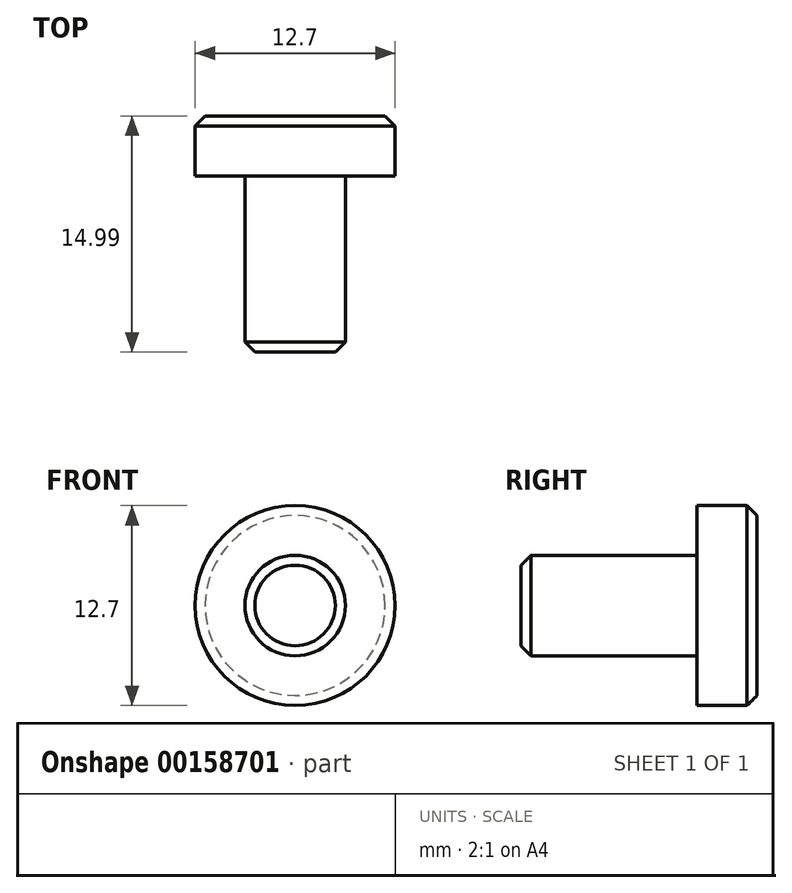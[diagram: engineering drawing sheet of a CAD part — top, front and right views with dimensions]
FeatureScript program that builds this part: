
annotation { "Feature Type Name" : "Feature", "Feature Type Description" : "" }
export const myFeature = defineFeature(function(context is Context, id is Id, definition is map)
    precondition{}
    {
        {
            var Q0;
            Q0=qCreatedBy(makeId("Right.planeOp"),FACE);
            var sketch = newSketch(context, id + "F0", { "sketchPlane" : qUnion([Q0])});
            skLineSegment(sketch, "E0", {"start": v(0, 0) * mm, "end": v(-14.99, 0) * mm});
            skLineSegment(sketch, "E1", {"start": v(-14.99, 0) * mm, "end": v(-14.99, 3.2) * mm});
            skLineSegment(sketch, "E2", {"start": v(-14.99, 3.2) * mm, "end": v(-3.8, 3.2) * mm});
            skLineSegment(sketch, "E3", {"start": v(-3.8, 3.2) * mm, "end": v(-3.8, 6.35) * mm});
            skLineSegment(sketch, "E4", {"start": v(-3.81, 6.35) * mm, "end": v(0, 6.35) * mm});
            skLineSegment(sketch, "E5", {"start": v(0, 6.35) * mm, "end": v(0, 0) * mm});
            skSolve(sketch);
        }
        {
            var Q0;
            Q0=makeQuery(id+"F0.imprint","IMPRINT",FACE,{"disambiguationData":[TD([[makeQuery(id+"F0.imprint","IMPRINT",EDGE,{"derivedFrom":sQuery(id+"F0.wireOp",EDGE,"E0")}),-1.0]])]});
            var Q1;
            Q1=sQuery(id+"F0.wireOp",EDGE,"E0");
            revolve(context, id + "F1", {"entities" : qUnion([Q0]), "axis" : qUnion([Q1]), "revolveType" : RevolveType.FULL});
        }
        {
            var Q0;
            Q0=makeQuery(id+"F1.opRevolve","SWEPT_FACE",FACE,{"disambiguationData":[OSD([sQuery(id+"F0.wireOp",EDGE,"E1")])]});
            var Q1;
            Q1=makeQuery(id+"F1.opRevolve","SWEPT_FACE",FACE,{"disambiguationData":[OSD([sQuery(id+"F0.wireOp",EDGE,"E5")])]});
            chamfer(context, id + "F2", {"entities" : qUnion([Q0, Q1]), "width" : 0.64 * mm, "tangentPropagation" : true});
        }
    });
